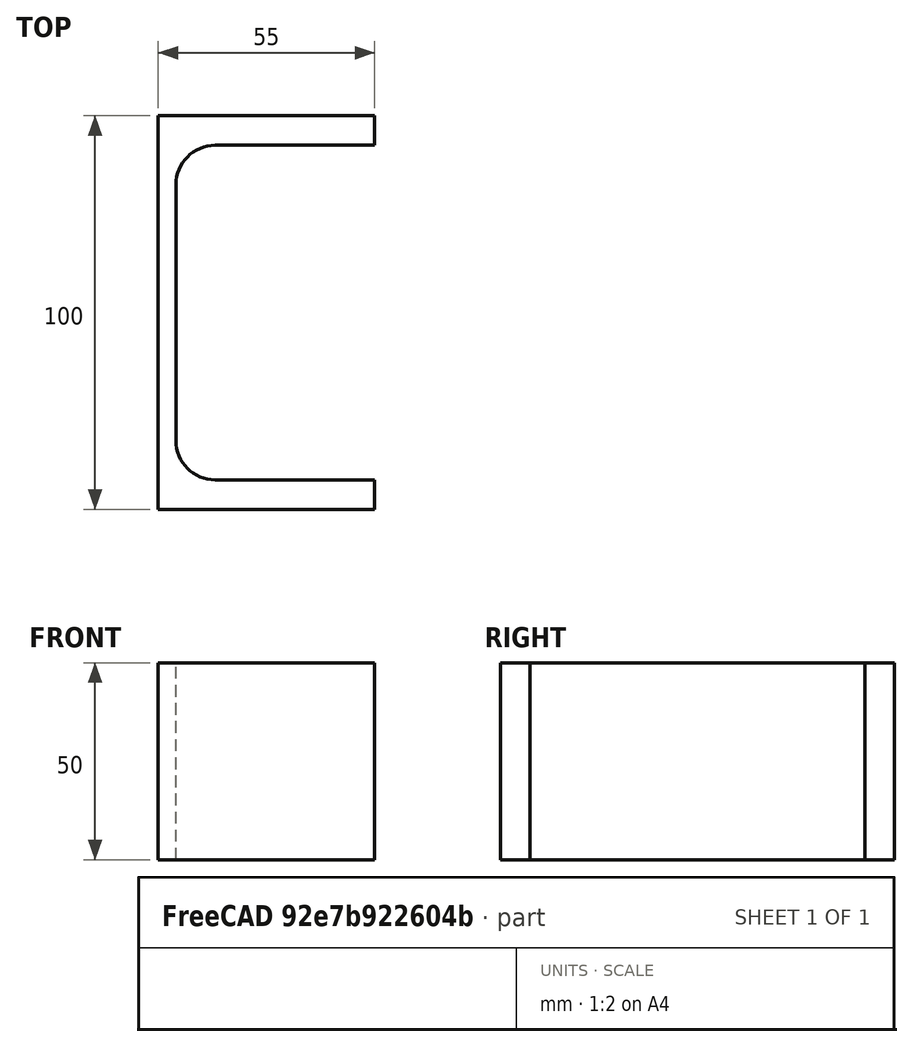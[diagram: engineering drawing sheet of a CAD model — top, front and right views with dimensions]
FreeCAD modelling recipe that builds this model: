
FCSTD DOCUMENT  (FreeCAD 0.20R29410 (Git))
Label: UPE-Profile 100 DIN1026-2 S235JR
License: All rights reserved
LicenseURL: http://en.wikipedia.org/wiki/All_rights_reserved
objects: Sketcher::SketchObject×1, Part::Extrusion×1
note: 2 computed .brp shape members not serialized (recipe doc carries the construction recipe); baked Part::Feature solids carry a one-line shape summary decoded from their .brp

FEATURE [Sketcher::SketchObject] Sketch
  FullyConstrained = true
  MapMode = 5
  sketch-geometry (10):
    g0: LineSegment StartX=4.5 StartY=-32.5 StartZ=0 EndX=4.5 EndY=32.5 EndZ=0
    g1: LineSegment StartX=14.5 StartY=42.5 StartZ=0 EndX=55 EndY=42.5 EndZ=0
    g2: LineSegment StartX=55 StartY=42.5 StartZ=0 EndX=55 EndY=50 EndZ=0
    g3: LineSegment StartX=55 StartY=-50 StartZ=0 EndX=55 EndY=-42.5 EndZ=0
    g4: LineSegment StartX=55 StartY=-42.5 StartZ=0 EndX=14.5 EndY=-42.5 EndZ=0
    g5: ArcOfCircle CenterX=14.5 CenterY=32.5 CenterZ=0 NormalX=0 NormalY=0 NormalZ=1 AngleXU=0 Radius=10 StartAngle=1.5708 EndAngle=3.14159
    g6: ArcOfCircle CenterX=14.5 CenterY=-32.5 CenterZ=0 NormalX=0 NormalY=0 NormalZ=1 AngleXU=0 Radius=10 StartAngle=3.14159 EndAngle=4.71239
    g7: LineSegment StartX=55 StartY=-50 StartZ=0 EndX=0 EndY=-50 EndZ=0
    g8: LineSegment StartX=0 StartY=-50 StartZ=0 EndX=0 EndY=50 EndZ=0
    g9: LineSegment StartX=0 StartY=50 StartZ=0 EndX=55 EndY=50 EndZ=0
  constraints (27):
    c: Vertical(g0)
    c: Coincident(g2,g1)
    c: Vertical(g2)
    c: Vertical(g3)
    c: Coincident(g4,g3)
    c: Horizontal(g4)
    c: Tangent(g1,g5) = 1.5708
    c: Tangent(g0,g5) = 1.5708
    c: Tangent(g0,g6) = 1.5708
    c: Tangent(g4,g6) = 1.5708
    c: Symmetric(g2,g3,g-1)
    c: DistanceY(g2) = 7.5
    c: Radius(g5) = 10
    c: Coincident(g3,g7)
    c: PointOnObject(g7,g-2)
    c: Horizontal(g7)
    c: Coincident(g7,g8)
    c: PointOnObject(g8,g-2)
    c: Coincident(g8,g9)
    c: Coincident(g9,g2)
    c: Horizontal(g9)
    c: Distance(g-1,g0) = 4.5
    c: DistanceX(g9,g9) = 55
    c: Horizontal(g1)
    c: Equal(g3,g2)
    c: Equal(g5,g6)
    c: DistanceY(g3,g2) = 100
FEATURE [Part::Extrusion] Extrude  label="IPE-Profile 100 DIN1026-2 S235JR"
  Base = -> Sketch
  Dir = (0,0,50)
  DirMode = 0
  FaceMakerClass = Part::FaceMakerExtrusion
  LengthFwd = 0
  LengthRev = 0
  Solid = true
  Symmetric = false
